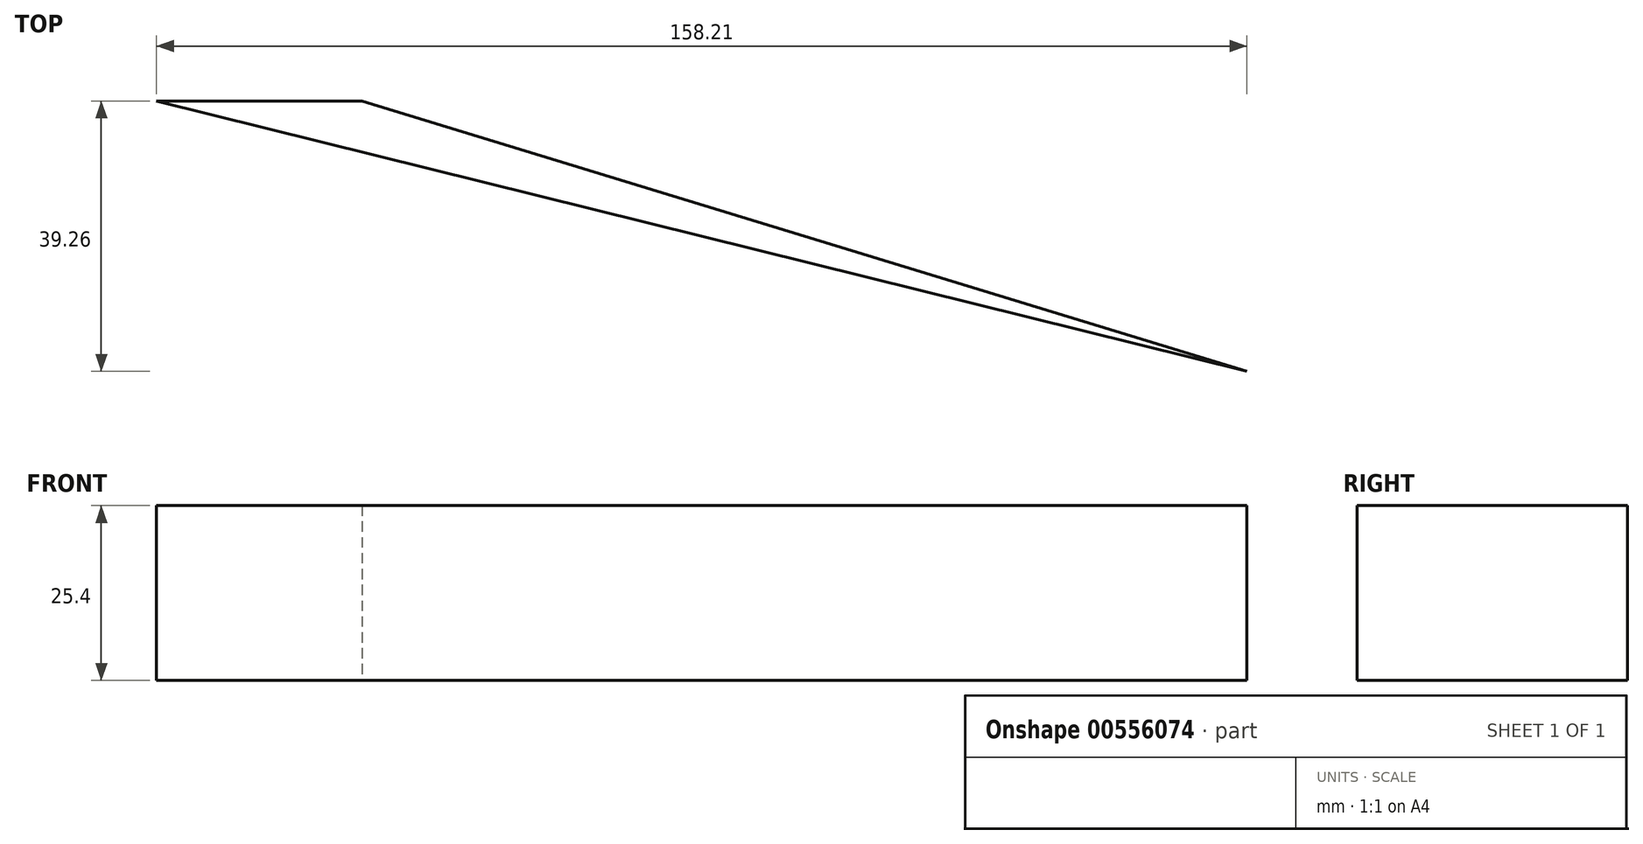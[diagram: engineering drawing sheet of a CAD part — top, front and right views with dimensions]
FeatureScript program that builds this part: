
annotation { "Feature Type Name" : "Feature", "Feature Type Description" : "" }
export const myFeature = defineFeature(function(context is Context, id is Id, definition is map)
    precondition{}
    {
        {
            var Q0;
            Q0=qCreatedBy(makeId("Top.planeOp"),FACE);
            var sketch = newSketch(context, id + "F0", { "sketchPlane" : qUnion([Q0])});
            skLineSegment(sketch, "E0.bottom", {"start": v(30.76, 30.85) * mm, "end": v(-30.76, 30.85) * mm});
            skLineSegment(sketch, "E0.top", {"start": v(30.76, -30.85) * mm, "end": v(-30.76, -30.85) * mm});
            skLineSegment(sketch, "E0.left", {"start": v(30.76, 30.85) * mm, "end": v(30.76, -30.85) * mm});
            skLineSegment(sketch, "E0.right", {"start": v(-30.76, 30.85) * mm, "end": v(-30.76, -30.85) * mm});
            skPoint(sketch, "E0.middle", {"position": v(0, 0) * mm});
            skSolve(sketch);
        }
        {
            var Q0;
            Q0 = qSketchRegion(id + "F0", true);
            var sketch = newSketch(context, id + "F1", { "sketchPlane" : qUnion([Q0])});
            skLineSegment(sketch, "E1", {"start": v(128.36, -24.73) * mm, "end": v(-29.84, 14.51) * mm});
            skLineSegment(sketch, "E2", {"start": v(-29.84, 14.51) * mm, "end": v(0, 14.51) * mm});
            skLineSegment(sketch, "E3", {"start": v(0, 14.51) * mm, "end": v(128.36, -24.73) * mm});
            skSolve(sketch);
        }
        {
            var Q0;
            Q0 = qSketchRegion(id + "F1", true);
            extrude(context, id + "F2", {"entities" : qUnion([Q0]), "depth" : 25.4 * mm, "offsetDistance" : 25.4 * mm});
        }
        {
            var Q0;
            Q0=makeQuery(id+"F2.opExtrude","SWEPT_FACE",FACE,{"disambiguationData":[OSD([sQuery(id+"F1.wireOp",EDGE,"E1")])]});
            extrude(context, id + "F3", {"entities" : qUnion([Q0]), "operationType" : NewBodyOperationType.ADD, "depth" : 1 / 50.8 * mm, "offsetDistance" : 25.4 * mm});
        }
    });
